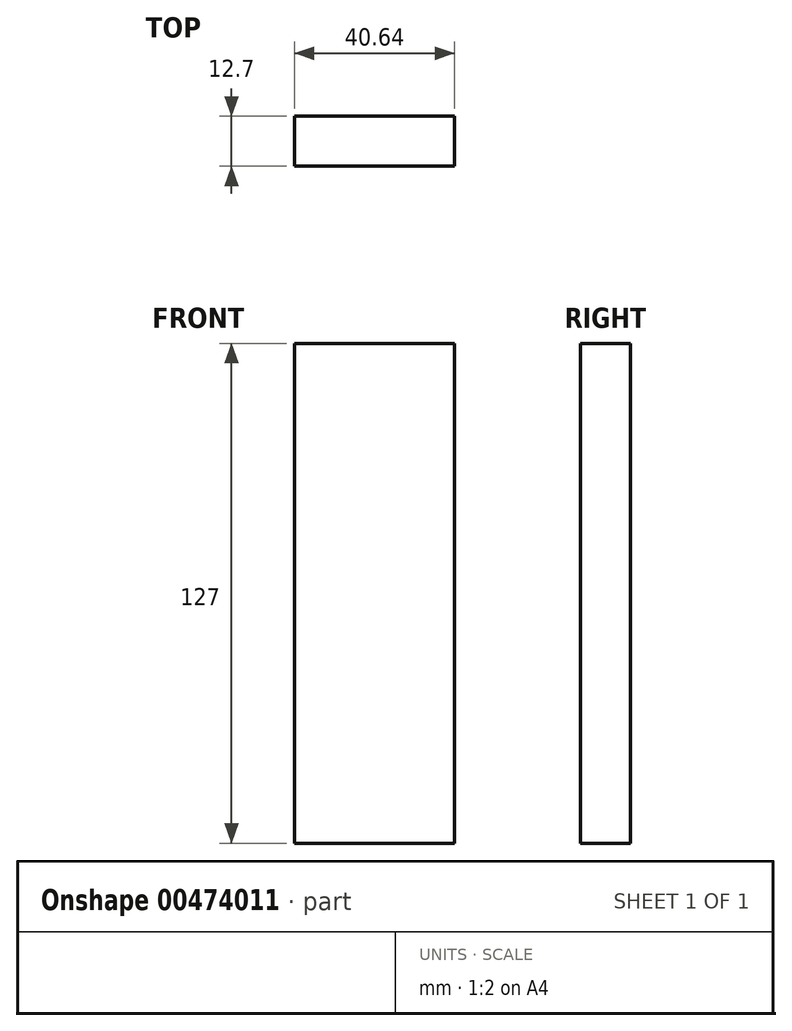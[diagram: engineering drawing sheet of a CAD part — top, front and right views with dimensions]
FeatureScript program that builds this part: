
annotation { "Feature Type Name" : "Feature", "Feature Type Description" : "" }
export const myFeature = defineFeature(function(context is Context, id is Id, definition is map)
    precondition{}
    {
        {
            var Q0;
            Q0=qCreatedBy(makeId("Front.planeOp"),FACE);
            var sketch = newSketch(context, id + "F0", { "sketchPlane" : qUnion([Q0])});
            skLineSegment(sketch, "E0.bottom", {"start": v(20.32, -63.5) * mm, "end": v(-20.32, -63.5) * mm});
            skLineSegment(sketch, "E0.top", {"start": v(20.32, 63.5) * mm, "end": v(-20.32, 63.5) * mm});
            skLineSegment(sketch, "E0.left", {"start": v(20.32, -63.5) * mm, "end": v(20.32, 63.5) * mm});
            skLineSegment(sketch, "E0.right", {"start": v(-20.32, -63.5) * mm, "end": v(-20.32, 63.5) * mm});
            skPoint(sketch, "E0.middle", {"position": v(0, 0) * mm});
            skSolve(sketch);
        }
        {
            var Q0;
            Q0=makeQuery(id+"F0.imprint","IMPRINT",FACE,{"disambiguationData":[TD([[makeQuery(id+"F0.imprint","IMPRINT",EDGE,{"derivedFrom":sQuery(id+"F0.wireOp",EDGE,"E0.bottom")}),-1.0]])]});
            var Q1;
            Q1 = qSketchRegion(id + "F2", true);
            extrude(context, id + "F1", {"entities" : qUnion([Q0, Q1]), "depth" : 12.7 * mm});
        }
    });
